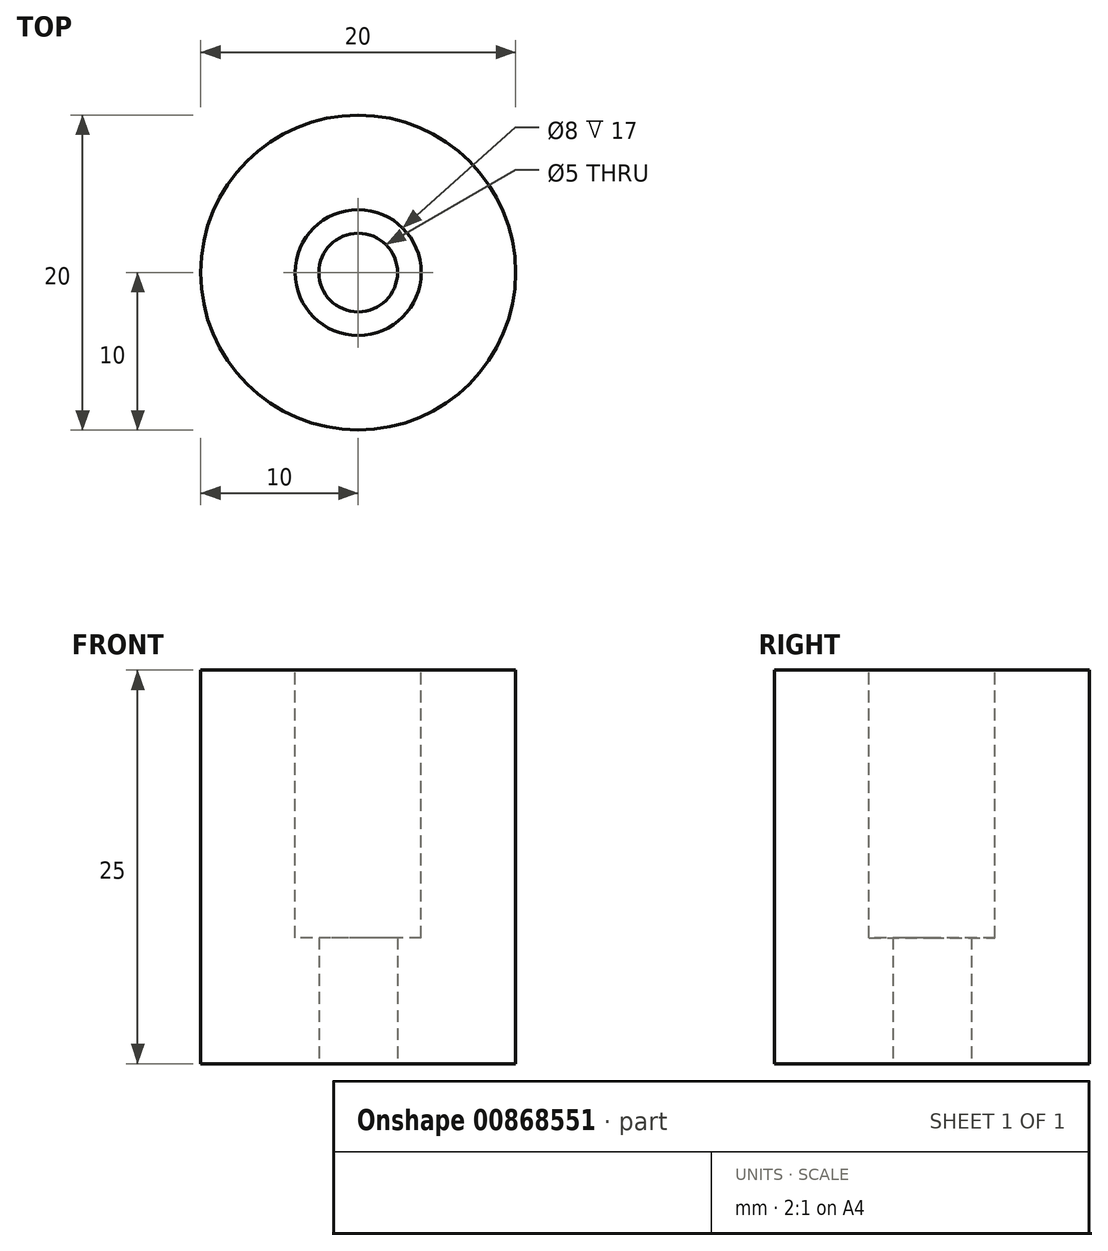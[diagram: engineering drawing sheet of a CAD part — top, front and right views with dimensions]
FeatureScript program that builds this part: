
annotation { "Feature Type Name" : "Feature", "Feature Type Description" : "" }
export const myFeature = defineFeature(function(context is Context, id is Id, definition is map)
    precondition{}
    {
        {
            var Q0;
            Q0=qCreatedBy(makeId("Top.planeOp"),FACE);
            var sketch = newSketch(context, id + "F0", { "sketchPlane" : qUnion([Q0])});
            skCircle(sketch, "E0", {"center": v(0, 0) * mm, "radius": 10 * mm});
            skSolve(sketch);
        }
        {
            var Q0;
            Q0=makeQuery(id+"F0.imprint","IMPRINT",FACE,{"disambiguationData":[TD([[makeQuery(id+"F0.imprint","IMPRINT",EDGE,{"derivedFrom":sQuery(id+"F0.wireOp",EDGE,"E0")}),1.0]])]});
            extrude(context, id + "F1", {"entities" : qUnion([Q0]), "depth" : 25 * mm, "offsetDistance" : 25 * mm});
        }
        {
            var Q0;
            Q0=makeQuery(id+"F1.opExtrude","CAP_FACE",FACE,{"disambiguationData":[OSD([sQuery(id+"F0.wireOp",EDGE,"E0")])],"isStart":false});
            var sketch = newSketch(context, id + "F2", { "sketchPlane" : qUnion([Q0])});
            skCircle(sketch, "E1", {"center": v(0, 0) * mm, "radius": 4 * mm});
            skSolve(sketch);
        }
        {
            var Q0;
            Q0 = qSketchRegion(id + "F2", true);
            extrude(context, id + "F3", {"entities" : qUnion([Q0]), "operationType" : NewBodyOperationType.REMOVE, "oppositeDirection" : true, "depth" : 17 * mm, "offsetDistance" : 25 * mm});
        }
        {
            var Q0;
            Q0=makeQuery(id+"F1.opExtrude","CAP_FACE",FACE,{"disambiguationData":[OSD([sQuery(id+"F0.wireOp",EDGE,"E0")])],"isStart":true});
            var sketch = newSketch(context, id + "F4", { "sketchPlane" : qUnion([Q0])});
            skCircle(sketch, "E2", {"center": v(0, 0) * mm, "radius": 2.5 * mm});
            skSolve(sketch);
        }
        {
            var Q0;
            Q0=makeQuery(id+"F4.imprint","IMPRINT",FACE,{"disambiguationData":[TD([[makeQuery(id+"F4.imprint","IMPRINT",EDGE,{"derivedFrom":sQuery(id+"F4.wireOp",EDGE,"E2")}),1.0]])]});
            extrude(context, id + "F5", {"entities" : qUnion([Q0]), "operationType" : NewBodyOperationType.REMOVE, "endBound" : BoundingType.THROUGH_ALL, "oppositeDirection" : true, "depth" : 25 * mm, "offsetDistance" : 25 * mm});
        }
    });
